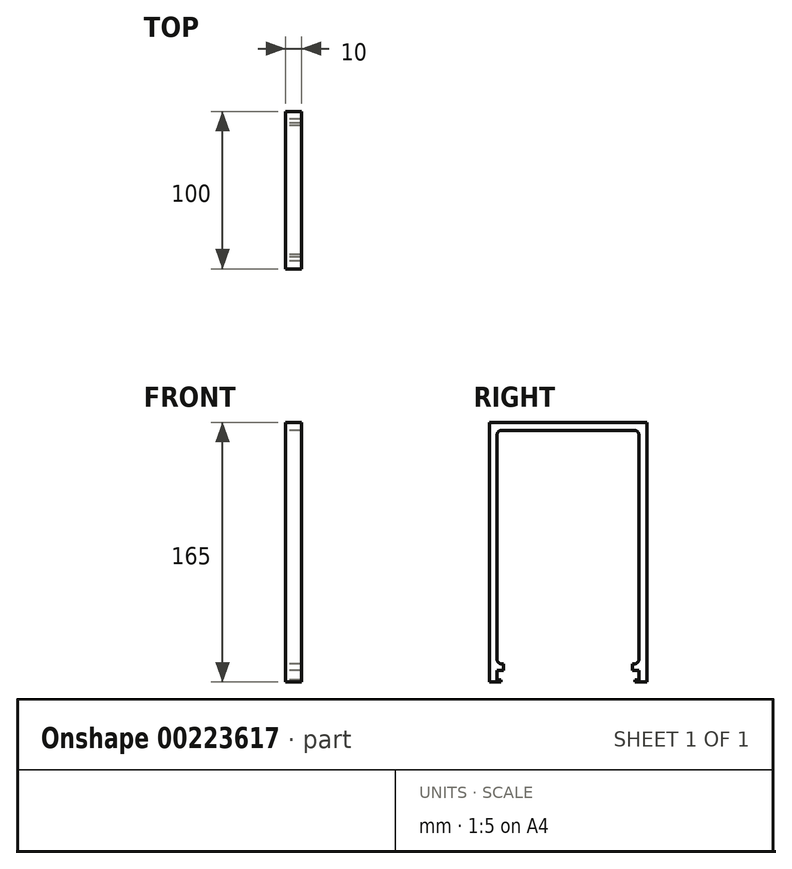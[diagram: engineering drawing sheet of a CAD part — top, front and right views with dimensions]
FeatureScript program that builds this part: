
annotation { "Feature Type Name" : "Feature", "Feature Type Description" : "" }
export const myFeature = defineFeature(function(context is Context, id is Id, definition is map)
    precondition{}
    {
        {
            var Q0;
            Q0=qCreatedBy(makeId("Right.planeOp"),FACE);
            var sketch = newSketch(context, id + "F0", { "sketchPlane" : qUnion([Q0])});
            skLineSegment(sketch, "E0", {"start": v(0, 0) * mm, "end": v(-50, 0) * mm});
            skLineSegment(sketch, "E1", {"start": v(-50, 0) * mm, "end": v(-50, -165) * mm});
            skLineSegment(sketch, "E2", {"start": v(-50, -165) * mm, "end": v(-42.5, -165) * mm});
            skLineSegment(sketch, "E3", {"start": v(-42.5, -165) * mm, "end": v(-42.5, -163.5) * mm});
            skLineSegment(sketch, "E4", {"start": v(-42.5, -163.5) * mm, "end": v(-45, -163.5) * mm});
            skLineSegment(sketch, "E5", {"start": v(-45, -163.5) * mm, "end": v(-45, -157.5) * mm});
            skLineSegment(sketch, "E6", {"start": v(-45, -157.5) * mm, "end": v(-41, -157.5) * mm});
            skLineSegment(sketch, "E7", {"start": v(-41, -157.5) * mm, "end": v(-41, -153.5) * mm});
            skLineSegment(sketch, "E8", {"start": v(-41, -153.5) * mm, "end": v(-45, -153.5) * mm});
            skLineSegment(sketch, "E9", {"start": v(-45, -153.5) * mm, "end": v(-45, -5) * mm});
            skLineSegment(sketch, "E10", {"start": v(-45, -5) * mm, "end": v(0, -5) * mm});
            skLineSegment(sketch, "E11", {"start": v(0, -5) * mm, "end": v(0, 0) * mm, "construction": true});
            skLineSegment(sketch, "E12.MirrorCS", {"start": v(42.5, -163.5) * mm, "end": v(45, -163.5) * mm});
            skLineSegment(sketch, "E13.MirrorCS", {"start": v(45, -163.5) * mm, "end": v(45, -157.5) * mm});
            skLineSegment(sketch, "E14.MirrorCS", {"start": v(41, -153.5) * mm, "end": v(45, -153.5) * mm});
            skLineSegment(sketch, "E15.MirrorCS", {"start": v(50, -165) * mm, "end": v(42.5, -165) * mm});
            skLineSegment(sketch, "E16.MirrorCS", {"start": v(42.5, -165) * mm, "end": v(42.5, -163.5) * mm});
            skLineSegment(sketch, "E17.MirrorCS", {"start": v(45, -157.5) * mm, "end": v(41, -157.5) * mm});
            skLineSegment(sketch, "E18.MirrorCS", {"start": v(41, -157.5) * mm, "end": v(41, -153.5) * mm});
            skLineSegment(sketch, "E19.MirrorCS", {"start": v(50, 0) * mm, "end": v(50, -165) * mm});
            skLineSegment(sketch, "E20.MirrorCS", {"start": v(45, -153.5) * mm, "end": v(45, -5) * mm});
            skLineSegment(sketch, "E21.MirrorCS", {"start": v(0, 0) * mm, "end": v(50, 0) * mm});
            skLineSegment(sketch, "E22.MirrorCS", {"start": v(45, -5) * mm, "end": v(0, -5) * mm});
            skSolve(sketch);
        }
        {
            var Q0;
            Q0 = qSketchRegion(id + "F0", true);
            extrude(context, id + "F1", {"entities" : qUnion([Q0]), "depth" : 10 * mm});
        }
        {
            var Q0;
            Q0=makeQuery(id+"F1.opExtrude","SWEPT_EDGE",EDGE,{"disambiguationData":[OSD([sQuery(id+"F0.wireOp",EDGE,"E9"),sQuery(id+"F0.wireOp",EDGE,"E10")])]});
            var Q1;
            Q1=makeQuery(id+"F1.opExtrude","SWEPT_EDGE",EDGE,{"disambiguationData":[OSD([sQuery(id+"F0.wireOp",EDGE,"E20.MirrorCS"),sQuery(id+"F0.wireOp",EDGE,"E22.MirrorCS")])]});
            var Q2;
            Q2=makeQuery(id+"F1.opExtrude","SWEPT_EDGE",EDGE,{"disambiguationData":[OSD([sQuery(id+"F0.wireOp",EDGE,"E14.MirrorCS"),sQuery(id+"F0.wireOp",EDGE,"E20.MirrorCS")])]});
            var Q3;
            Q3=makeQuery(id+"F1.opExtrude","SWEPT_EDGE",EDGE,{"disambiguationData":[OSD([sQuery(id+"F0.wireOp",EDGE,"E8"),sQuery(id+"F0.wireOp",EDGE,"E9")])]});
            fillet(context, id + "F2", {"entities" : qUnion([Q0, Q1, Q2, Q3]), "radius" : 3 * mm, "tangentPropagation" : true, "allowEdgeOverflow" : false});
        }
    });
